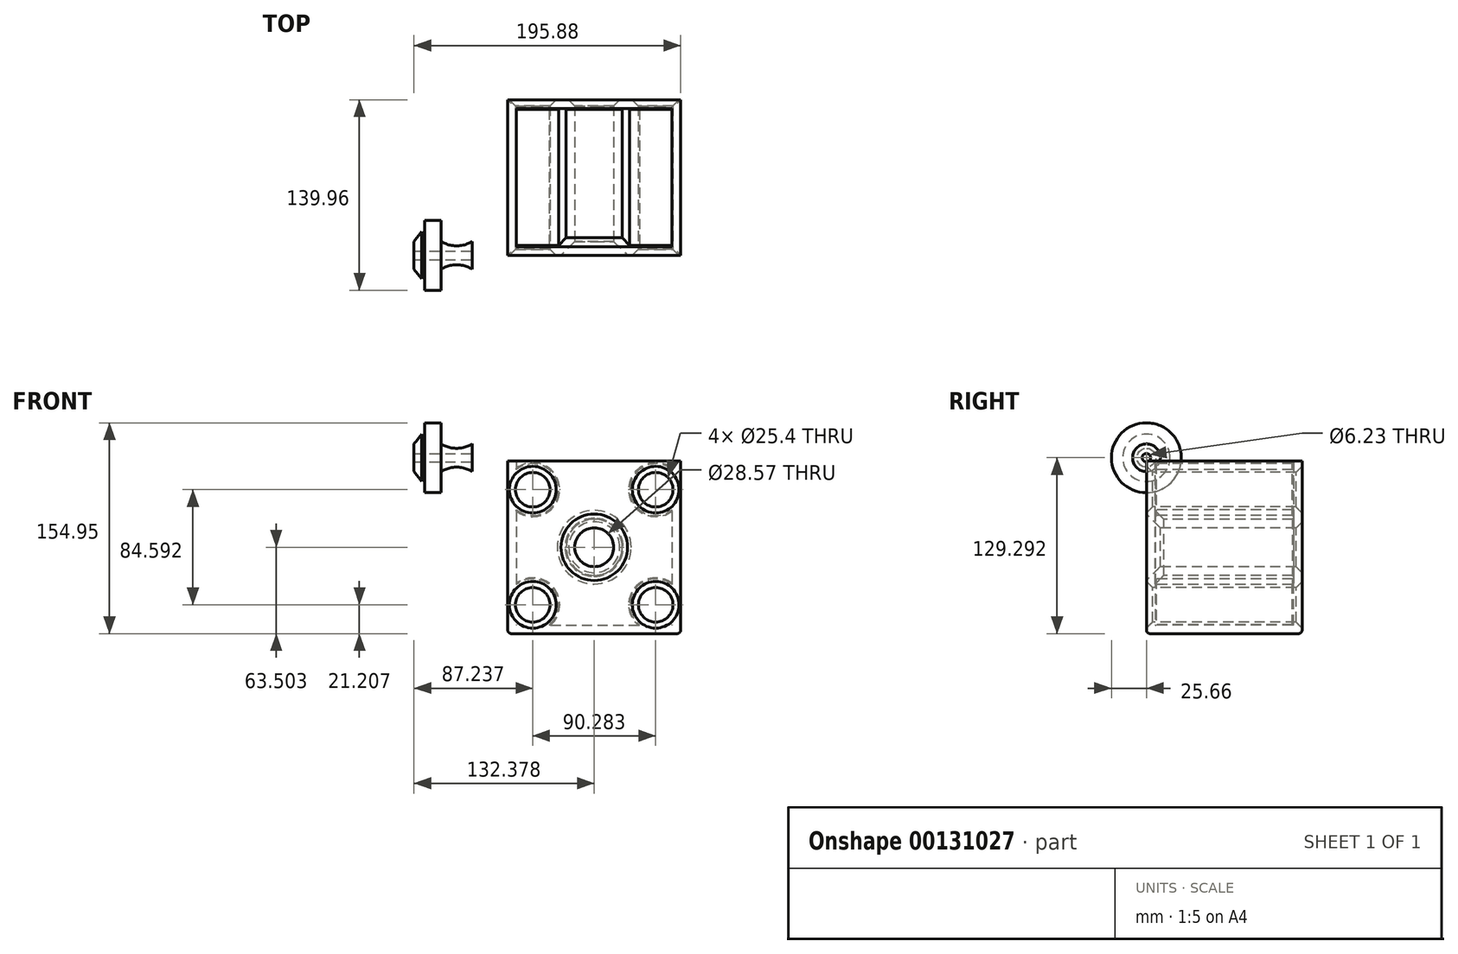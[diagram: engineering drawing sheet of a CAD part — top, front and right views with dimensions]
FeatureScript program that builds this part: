
annotation { "Feature Type Name" : "Feature", "Feature Type Description" : "" }
export const myFeature = defineFeature(function(context is Context, id is Id, definition is map)
    precondition{}
    {
        {
            var Q0;
            Q0=qCreatedBy(makeId("Front.planeOp"),FACE);
            var sketch = newSketch(context, id + "F0", { "sketchPlane" : qUnion([Q0])});
            skLineSegment(sketch, "E0.bottom", {"start": v(-73.1, 36.2) * mm, "end": v(53.9, 36.2) * mm});
            skLineSegment(sketch, "E0.top", {"start": v(-73.1, -90.8) * mm, "end": v(53.9, -90.8) * mm});
            skLineSegment(sketch, "E0.left", {"start": v(-73.1, 36.2) * mm, "end": v(-73.1, -90.8) * mm});
            skLineSegment(sketch, "E0.right", {"start": v(53.9, 36.2) * mm, "end": v(53.9, -90.8) * mm});
            skLineSegment(sketch, "E1", {"start": v(-73.1, 36.2) * mm, "end": v(-9.6, 80.66) * mm});
            skPoint(sketch, "E1.endSnap0", {"position": v(-9.6, 36.2) * mm});
            skLineSegment(sketch, "E2", {"start": v(-9.6, 80.66) * mm, "end": v(53.9, 36.2) * mm});
            skCircle(sketch, "E3", {"center": v(-9.6, -27.3) * mm, "radius": 14.29 * mm});
            skArc(sketch, "E4", {"start": v(-73.1, -90.8) * mm, "mid": v(-9.6, -154.3) * mm, "end": v(53.9, -90.8) * mm});
            skCircle(sketch, "E5", {"center": v(-54.73, 14.99) * mm, "radius": 12.7 * mm});
            skLineSegment(sketch, "E6", {"start": v(-73.1, -27.3) * mm, "end": v(53.9, -27.3) * mm, "construction": true});
            skCircle(sketch, "E7.MirrorC", {"center": v(-54.73, -69.6) * mm, "radius": 12.7 * mm});
            skLineSegment(sketch, "E8", {"start": v(-9.6, 80.66) * mm, "end": v(-9.6, -154.3) * mm, "construction": true});
            skCircle(sketch, "E9.MirrorC", {"center": v(35.55, 14.99) * mm, "radius": 12.7 * mm});
            skCircle(sketch, "E10.MirrorC", {"center": v(35.55, -69.6) * mm, "radius": 12.7 * mm});
            skSolve(sketch);
        }
        {
            var Q0;
            Q0=makeQuery(id+"F0.imprint","IMPRINT",FACE,{"disambiguationData":[TD([[makeQuery(id+"F0.imprint","IMPRINT",EDGE,{"derivedFrom":sQuery(id+"F0.wireOp",EDGE,"E0.bottom")}),-1.0]])]});
            var Q1;
            Q1=sQuery(id+"F0.wireOp",EDGE,"E1");
            var Q2;
            Q2=sQuery(id+"F0.wireOp",EDGE,"E2");
            var Q3;
            Q3=sQuery(id+"F0.wireOp",EDGE,"E0.right");
            var Q4;
            Q4=sQuery(id+"F0.wireOp",EDGE,"E4");
            var Q5;
            Q5=sQuery(id+"F0.wireOp",EDGE,"E0.left");
            extrude(context, id + "F1", {"entities" : qUnion([Q0]), "surfaceEntities" : qUnion([Q1, Q2, Q3, Q4, Q5]), "oppositeDirection" : true, "depth" : 114.3 * mm});
        }
        {
            var Q0;
            Q0=makeQuery(id+"F1.opExtrude","SWEPT_EDGE",EDGE,{"disambiguationData":[OSD([sQuery(id+"F0.wireOp",EDGE,"E0.top"),sQuery(id+"F0.wireOp",EDGE,"E0.right"),sQuery(id+"F0.wireOp",EDGE,"E4")])]});
            var Q1;
            Q1=makeQuery(id+"F1.opExtrude","CAP_EDGE",EDGE,{"disambiguationData":[OSD([sQuery(id+"F0.wireOp",EDGE,"E0.top")])],"isStart":true});
            var Q2;
            Q2=makeQuery(id+"F1.opExtrude","CAP_EDGE",EDGE,{"disambiguationData":[OSD([sQuery(id+"F0.wireOp",EDGE,"E0.top")])],"isStart":false});
            var Q3;
            Q3=makeQuery(id+"F1.opExtrude","SWEPT_EDGE",EDGE,{"disambiguationData":[OSD([sQuery(id+"F0.wireOp",EDGE,"E0.top"),sQuery(id+"F0.wireOp",EDGE,"E0.left"),sQuery(id+"F0.wireOp",EDGE,"E4")])]});
            fillet(context, id + "F2", {"entities" : qUnion([Q0, Q1, Q2, Q3]), "radius" : 2.54 * mm, "tangentPropagation" : true, "allowEdgeOverflow" : false});
        }
        {
            var Q0;
            Q0=makeQuery(id+"F1.opExtrude","CAP_EDGE",EDGE,{"disambiguationData":[OSD([sQuery(id+"F0.wireOp",EDGE,"E5")])],"isStart":true});
            var Q1;
            Q1=makeQuery(id+"F1.opExtrude","CAP_EDGE",EDGE,{"disambiguationData":[OSD([sQuery(id+"F0.wireOp",EDGE,"E7.MirrorC")])],"isStart":true});
            var Q2;
            Q2=makeQuery(id+"F1.opExtrude","CAP_EDGE",EDGE,{"disambiguationData":[OSD([sQuery(id+"F0.wireOp",EDGE,"E10.MirrorC")])],"isStart":true});
            var Q3;
            Q3=makeQuery(id+"F1.opExtrude","CAP_EDGE",EDGE,{"disambiguationData":[OSD([sQuery(id+"F0.wireOp",EDGE,"E9.MirrorC")])],"isStart":true});
            var Q4;
            Q4=makeQuery(id+"F1.opExtrude","CAP_EDGE",EDGE,{"disambiguationData":[OSD([sQuery(id+"F0.wireOp",EDGE,"E9.MirrorC")])],"isStart":false});
            var Q5;
            Q5=makeQuery(id+"F1.opExtrude","CAP_EDGE",EDGE,{"disambiguationData":[OSD([sQuery(id+"F0.wireOp",EDGE,"E5")])],"isStart":false});
            var Q6;
            Q6=makeQuery(id+"F1.opExtrude","CAP_EDGE",EDGE,{"disambiguationData":[OSD([sQuery(id+"F0.wireOp",EDGE,"E3")])],"isStart":false});
            var Q7;
            Q7=makeQuery(id+"F1.opExtrude","CAP_EDGE",EDGE,{"disambiguationData":[OSD([sQuery(id+"F0.wireOp",EDGE,"E10.MirrorC")])],"isStart":false});
            var Q8;
            Q8=makeQuery(id+"F1.opExtrude","CAP_EDGE",EDGE,{"disambiguationData":[OSD([sQuery(id+"F0.wireOp",EDGE,"E7.MirrorC")])],"isStart":false});
            chamfer(context, id + "F3", {"entities" : qUnion([Q0, Q1, Q2, Q3, Q4, Q5, Q6, Q7, Q8]), "width" : 4.44 * mm, "tangentPropagation" : true});
        }
        {
            var Q0;
            Q0=makeQuery(id+"F1.opExtrude","CAP_EDGE",EDGE,{"disambiguationData":[OSD([sQuery(id+"F0.wireOp",EDGE,"E3")])],"isStart":true});
            chamfer(context, id + "F4", {"entities" : qUnion([Q0]), "width" : 10.16 * mm, "tangentPropagation" : true});
        }
        {
            var Q0;
            Q0=makeQuery(id+"F1.opExtrude","SWEPT_FACE",FACE,{"disambiguationData":[OSD([sQuery(id+"F0.wireOp",EDGE,"E0.bottom")])]});
            shell(context, id + "F5", {"entities" : qUnion([Q0]), "thickness" : 6.35 * mm});
        }
        {
            var Q0;
            Q0=qCreatedBy(makeId("Front.planeOp"),FACE);
            var sketch = newSketch(context, id + "F6", { "sketchPlane" : qUnion([Q0])});
            skLineSegment(sketch, "E11.top", {"start": v(-141.97, 38.48) * mm, "end": v(-99.33, 38.48) * mm});
            skLineSegment(sketch, "E11.left", {"start": v(-141.97, 48.63) * mm, "end": v(-141.97, 38.48) * mm});
            skLineSegment(sketch, "E11.right", {"start": v(-99.33, 48.63) * mm, "end": v(-99.33, 38.48) * mm});
            skLineSegment(sketch, "E12", {"start": v(-141.97, 48.63) * mm, "end": v(-136.33, 55.84) * mm});
            skLineSegment(sketch, "E13", {"start": v(-136.33, 55.84) * mm, "end": v(-134.21, 48.63) * mm});
            skLineSegment(sketch, "E14", {"start": v(-134.21, 48.63) * mm, "end": v(-134.21, 64.14) * mm});
            skLineSegment(sketch, "E15", {"start": v(-134.21, 64.14) * mm, "end": v(-122, 64.14) * mm});
            skLineSegment(sketch, "E16", {"start": v(-122, 64.14) * mm, "end": v(-122, 48.63) * mm});
            skArc(sketch, "E17", {"start": v(-122, 48.63) * mm, "mid": v(-110.67, 45.42) * mm, "end": v(-99.33, 48.63) * mm});
            skSolve(sketch);
        }
        {
            var Q0;
            Q0 = qSketchRegion(id + "F6", true);
            var Q1;
            Q1=sQuery(id+"F6.wireOp",EDGE,"E11.top");
            revolve(context, id + "F7", {"entities" : qUnion([Q0]), "axis" : qUnion([Q1]), "revolveType" : RevolveType.FULL});
        }
        {
            var Q0;
            Q0=makeQuery(id+"F7.opRevolve","SWEPT_FACE",FACE,{"disambiguationData":[OSD([sQuery(id+"F6.wireOp",EDGE,"E11.right")])]});
            var sketch = newSketch(context, id + "F8", { "sketchPlane" : qUnion([Q0])});
            skCircle(sketch, "E18", {"center": v(0, 38.48) * mm, "radius": 3.11 * mm});
            skSolve(sketch);
        }
        {
            var Q0;
            Q0 = qSketchRegion(id + "F8", true);
            extrude(context, id + "F9", {"entities" : qUnion([Q0]), "operationType" : NewBodyOperationType.REMOVE, "endBound" : BoundingType.THROUGH_ALL, "oppositeDirection" : true, "depth" : 25.4 * mm});
        }
    });
